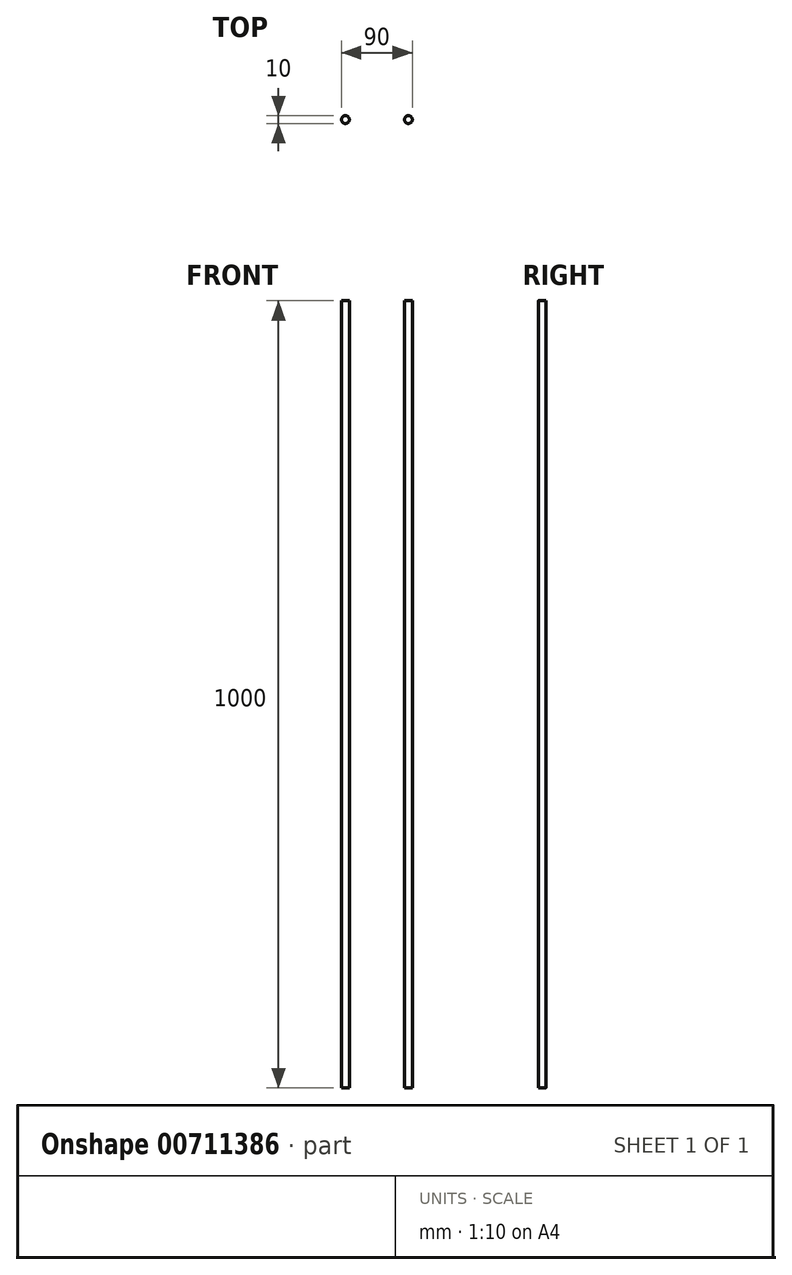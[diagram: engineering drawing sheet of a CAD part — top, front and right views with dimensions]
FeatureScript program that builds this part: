
annotation { "Feature Type Name" : "Feature", "Feature Type Description" : "" }
export const myFeature = defineFeature(function(context is Context, id is Id, definition is map)
    precondition{}
    {
        {
            var Q0;
            Q0=qCreatedBy(makeId("Top.planeOp"),FACE);
            var sketch = newSketch(context, id + "F0", { "sketchPlane" : qUnion([Q0])});
            skCircle(sketch, "E0", {"center": v(-40, 0) * mm, "radius": 5 * mm});
            skCircle(sketch, "E1", {"center": v(40, 0) * mm, "radius": 5 * mm});
            skSolve(sketch);
        }
        {
            var Q0;
            Q0 = qSketchRegion(id + "F0", true);
            extrude(context, id + "F1", {"entities" : qUnion([Q0]), "depth" : 1000 * mm, "offsetDistance" : 25 * mm});
        }
    });
